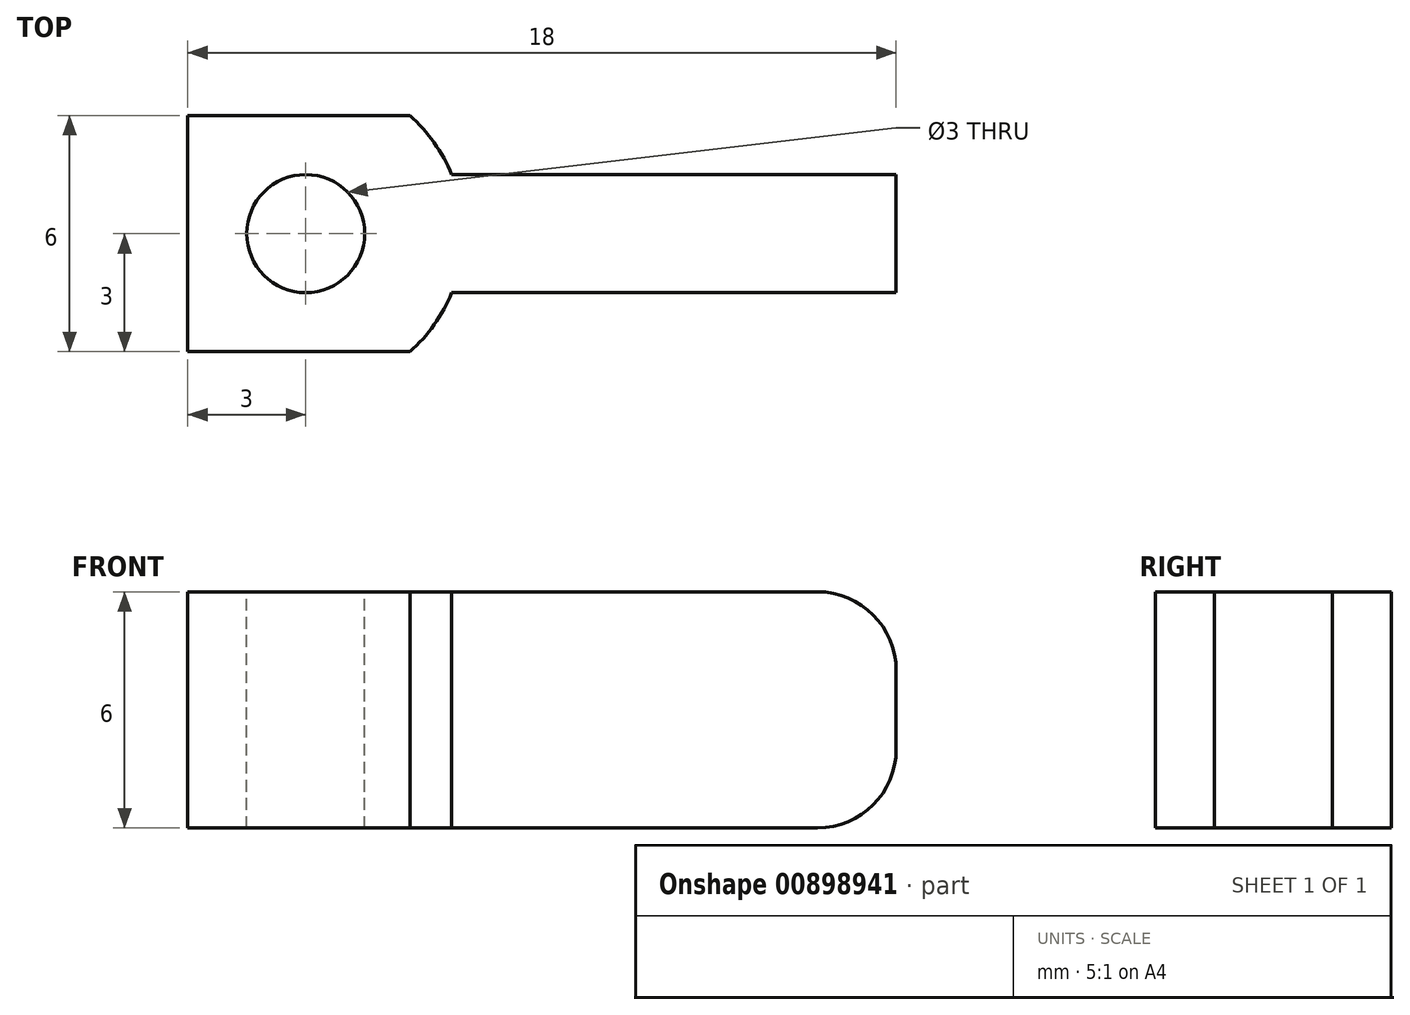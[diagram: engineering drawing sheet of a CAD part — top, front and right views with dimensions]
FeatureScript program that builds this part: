
annotation { "Feature Type Name" : "Feature", "Feature Type Description" : "" }
export const myFeature = defineFeature(function(context is Context, id is Id, definition is map)
    precondition{}
    {
        {
            var Q0;
            Q0=qCreatedBy(makeId("Top.planeOp"),FACE);
            var sketch = newSketch(context, id + "F0", { "sketchPlane" : qUnion([Q0])});
            skLineSegment(sketch, "E0.bottom", {"start": v(-3, 3) * mm, "end": v(15, 3) * mm});
            skLineSegment(sketch, "E0.top", {"start": v(-3, -3) * mm, "end": v(15, -3) * mm});
            skLineSegment(sketch, "E0.left", {"start": v(-3, 3) * mm, "end": v(-3, -3) * mm});
            skLineSegment(sketch, "E0.right", {"start": v(15, 3) * mm, "end": v(15, -3) * mm});
            skSolve(sketch);
        }
        {
            var Q0;
            Q0 = qSketchRegion(id + "F0", true);
            extrude(context, id + "F1", {"entities" : qUnion([Q0]), "depth" : 6 * mm, "offsetDistance" : 25 * mm});
        }
        {
            var Q0;
            Q0=makeQuery(id+"F1.opExtrude","CAP_FACE",FACE,{"disambiguationData":[OSD([sQuery(id+"F0.wireOp",EDGE,"E0.bottom"),sQuery(id+"F0.wireOp",EDGE,"E0.top"),sQuery(id+"F0.wireOp",EDGE,"E0.left"),sQuery(id+"F0.wireOp",EDGE,"E0.right")])],"isStart":false});
            var sketch = newSketch(context, id + "F2", { "sketchPlane" : qUnion([Q0])});
            skCircle(sketch, "E1", {"center": v(0, 0) * mm, "radius": 1.5 * mm});
            skSolve(sketch);
        }
        {
            var Q0;
            Q0 = qSketchRegion(id + "F2", true);
            extrude(context, id + "F3", {"entities" : qUnion([Q0]), "operationType" : NewBodyOperationType.REMOVE, "oppositeDirection" : true, "depth" : 10 * mm, "offsetDistance" : 25 * mm});
        }
        {
            var Q0;
            Q0=makeQuery(id+"F1.opExtrude","CAP_FACE",FACE,{"disambiguationData":[OSD([sQuery(id+"F0.wireOp",EDGE,"E0.bottom"),sQuery(id+"F0.wireOp",EDGE,"E0.top"),sQuery(id+"F0.wireOp",EDGE,"E0.left"),sQuery(id+"F0.wireOp",EDGE,"E0.right")])],"isStart":false});
            var sketch = newSketch(context, id + "F4", { "sketchPlane" : qUnion([Q0])});
            skLineSegment(sketch, "E2.0", {"start": v(15, -1.5) * mm, "end": v(3.7, -1.5) * mm});
            skLineSegment(sketch, "E3.0", {"start": v(15, 1.5) * mm, "end": v(3.7, 1.5) * mm});
            skArc(sketch, "E4", {"start": v(2.65, -3) * mm, "mid": v(3.26, -2.31) * mm, "end": v(3.7, -1.5) * mm});
            skPoint(sketch, "E5.orphan", {"position": v(0, 3) * mm});
            skArc(sketch, "E6.trimOffspring", {"start": v(3.7, 1.5) * mm, "mid": v(3.26, 2.31) * mm, "end": v(2.65, 3) * mm});
            skLineSegment(sketch, "E7", {"start": v(15, 1.5) * mm, "end": v(15, 3) * mm});
            skLineSegment(sketch, "E8", {"start": v(15, -1.5) * mm, "end": v(15, -3) * mm});
            skLineSegment(sketch, "E9.trimOffspring", {"start": v(2.65, -3) * mm, "end": v(15, -3) * mm});
            skPoint(sketch, "E10.1.start.orphan", {"position": v(-3, -3) * mm});
            skLineSegment(sketch, "E11.trimOffspring", {"start": v(2.65, 3) * mm, "end": v(15, 3) * mm});
            skPoint(sketch, "E10.0.start.orphan", {"position": v(-3, 3) * mm});
            skSolve(sketch);
        }
        {
            var Q0;
            Q0=makeQuery(id+"F4.imprint","IMPRINT",FACE,{"disambiguationData":[TD([[makeQuery(id+"F4.imprint","IMPRINT",EDGE,{"derivedFrom":sQuery(id+"F4.wireOp",EDGE,"E3.0")}),-1.0]])]});
            var Q1;
            Q1=makeQuery(id+"F4.imprint","IMPRINT",FACE,{"disambiguationData":[TD([[makeQuery(id+"F4.imprint","IMPRINT",EDGE,{"derivedFrom":sQuery(id+"F4.wireOp",EDGE,"E2.0")}),1.0]])]});
            extrude(context, id + "F5", {"entities" : qUnion([Q0, Q1]), "operationType" : NewBodyOperationType.REMOVE, "oppositeDirection" : true, "depth" : 25 * mm, "offsetDistance" : 25 * mm});
        }
        {
            var Q0;
            Q0=makeQuery(id+"F1.opExtrude","CAP_EDGE",EDGE,{"disambiguationData":[OSD([sQuery(id+"F0.wireOp",EDGE,"E0.right")])],"isStart":false});
            var Q1;
            Q1=makeQuery(id+"F1.opExtrude","CAP_EDGE",EDGE,{"disambiguationData":[OSD([sQuery(id+"F0.wireOp",EDGE,"E0.right")])],"isStart":true});
            fillet(context, id + "F6", {"entities" : qUnion([Q0, Q1]), "radius" : 2 * mm, "tangentPropagation" : true, "allowEdgeOverflow" : false});
        }
    });
